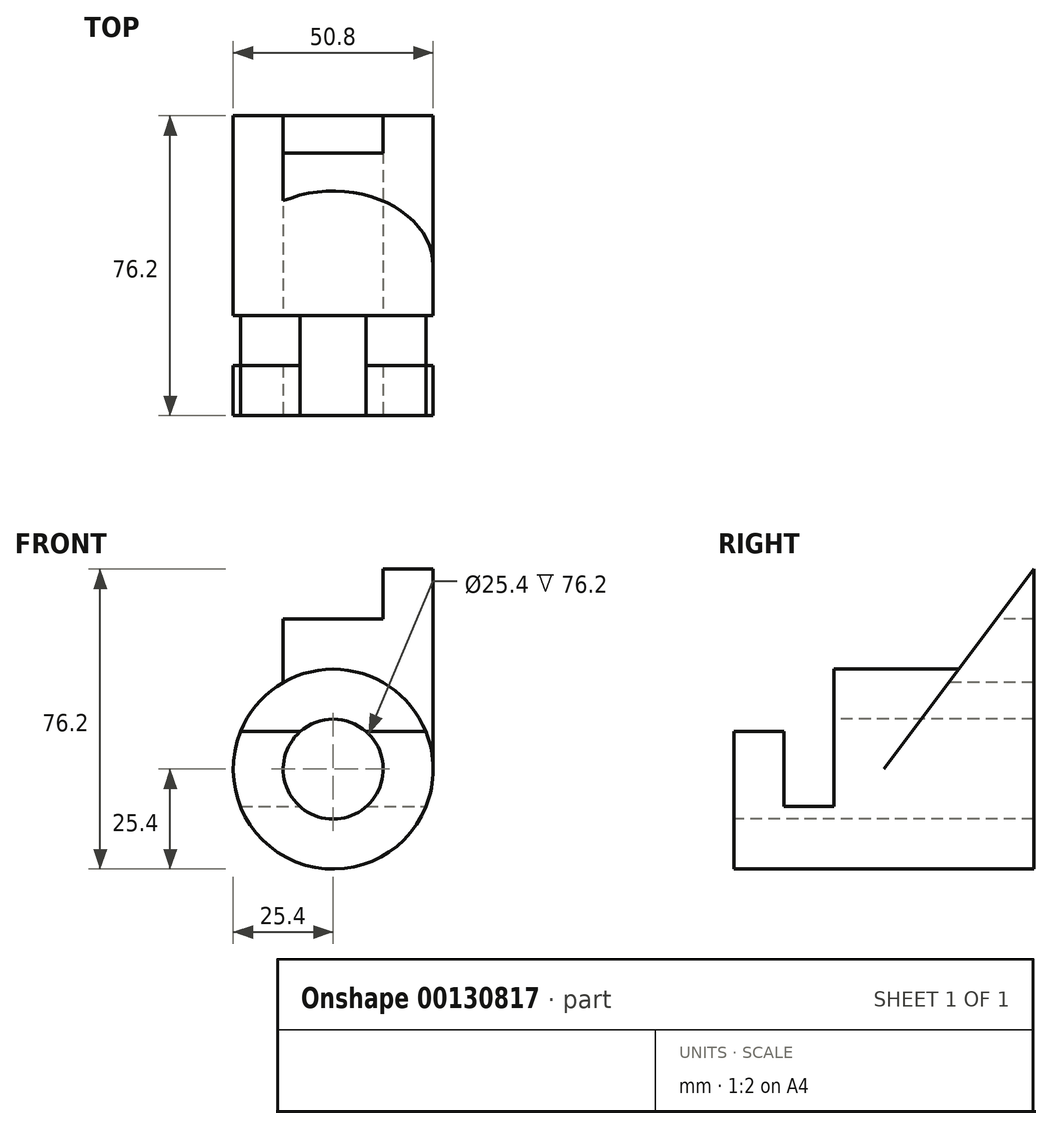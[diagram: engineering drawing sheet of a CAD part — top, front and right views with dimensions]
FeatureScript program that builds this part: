
annotation { "Feature Type Name" : "Feature", "Feature Type Description" : "" }
export const myFeature = defineFeature(function(context is Context, id is Id, definition is map)
    precondition{}
    {
        {
            var Q0;
            Q0=qCreatedBy(makeId("Front.planeOp"),FACE);
            var sketch = newSketch(context, id + "F0", { "sketchPlane" : qUnion([Q0])});
            skCircle(sketch, "E0", {"center": v(0, 0) * mm, "radius": 12.7 * mm});
            skCircle(sketch, "E1", {"center": v(0, 0) * mm, "radius": 25.4 * mm});
            skLineSegment(sketch, "E2", {"start": v(-8.4, 9.53) * mm, "end": v(-23.55, 9.53) * mm});
            skLineSegment(sketch, "E3.trimOffspring", {"start": v(8.4, 9.53) * mm, "end": v(23.55, 9.53) * mm});
            skLineSegment(sketch, "E4", {"start": v(-23.55, -9.53) * mm, "end": v(-8.4, -9.53) * mm});
            skLineSegment(sketch, "E5.trimOffspring", {"start": v(8.4, -9.53) * mm, "end": v(23.55, -9.53) * mm});
            skSolve(sketch);
        }
        {
            var Q0;
            {var subQ0=sQuery(id+"F0.wireOp",EDGE,"E2");Q0=makeQuery(id+"F0.imprint","IMPRINT",FACE,{"disambiguationData":[TD([[makeQuery(id+"F0.imprint","IMPRINT",EDGE,{"derivedFrom":subQ0}),1.0]])]});}
            var Q1;
            {var subQ0=sQuery(id+"F0.wireOp",EDGE,"E4");Q1=makeQuery(id+"F0.imprint","IMPRINT",FACE,{"disambiguationData":[TD([[makeQuery(id+"F0.imprint","IMPRINT",EDGE,{"derivedFrom":subQ0}),-1.0]])]});}
            var Q2;
            {var subQ0=sQuery(id+"F0.wireOp",EDGE,"E3.trimOffspring");Q2=makeQuery(id+"F0.imprint","IMPRINT",FACE,{"disambiguationData":[TD([[makeQuery(id+"F0.imprint","IMPRINT",EDGE,{"derivedFrom":subQ0}),-1.0]])]});}
            var Q3;
            {var subQ0=sQuery(id+"F0.wireOp",EDGE,"E2");Q3=makeQuery(id+"F0.imprint","IMPRINT",FACE,{"disambiguationData":[TD([[makeQuery(id+"F0.imprint","IMPRINT",EDGE,{"derivedFrom":subQ0}),-1.0]])]});}
            extrude(context, id + "F1", {"entities" : qUnion([Q0, Q1, Q2, Q3]), "oppositeDirection" : true, "depth" : 76.2 * mm});
        }
        {
            var Q0;
            Q0=qCreatedBy(makeId("Right.planeOp"),FACE);
            var sketch = newSketch(context, id + "F2", { "sketchPlane" : qUnion([Q0])});
            skLineSegment(sketch, "E6", {"start": v(0, 25.4) * mm, "end": v(76.2, 25.4) * mm});
            skLineSegment(sketch, "E7", {"start": v(76.2, -25.4) * mm, "end": v(0, -25.4) * mm});
            skLineSegment(sketch, "E8.0", {"start": v(0, -25.4) * mm, "end": v(0, 25.4) * mm});
            skLineSegment(sketch, "E9", {"start": v(25.4, 25.4) * mm, "end": v(25.4, -9.53) * mm});
            skLineSegment(sketch, "E10", {"start": v(25.4, -9.53) * mm, "end": v(12.7, -9.53) * mm});
            skLineSegment(sketch, "E11", {"start": v(12.7, -9.53) * mm, "end": v(12.7, 9.53) * mm});
            skLineSegment(sketch, "E12", {"start": v(12.7, 9.53) * mm, "end": v(0, 9.53) * mm});
            skSolve(sketch);
        }
        {
            var Q0;
            {var subQ4=sQuery(id+"F2.wireOp",EDGE,"E9");Q0=makeQuery(id+"F2.imprint","IMPRINT",FACE,{"disambiguationData":[TD([[makeQuery(id+"F2.imprint","IMPRINT",EDGE,{"derivedFrom":subQ4}),-1.0]])]});}
            extrude(context, id + "F3", {"entities" : qUnion([Q0]), "operationType" : NewBodyOperationType.REMOVE, "endBound" : BoundingType.SYMMETRIC, "oppositeDirection" : true, "depth" : 50.8 * mm});
        }
        {
            var Q0;
            Q0=qCreatedBy(makeId("Right.planeOp"),FACE);
            var sketch = newSketch(context, id + "F4", { "sketchPlane" : qUnion([Q0])});
            skLineSegment(sketch, "E13.0", {"start": v(76.2, -25.4) * mm, "end": v(76.2, 25.4) * mm});
            skLineSegment(sketch, "E14", {"start": v(76.2, 0) * mm, "end": v(76.2, 50.8) * mm});
            skLineSegment(sketch, "E15", {"start": v(76.2, 0) * mm, "end": v(38.1, 0) * mm});
            skLineSegment(sketch, "E16", {"start": v(38.1, 0) * mm, "end": v(76.2, 50.8) * mm});
            skSolve(sketch);
        }
        {
            var Q0;
            {var subQ0=sQuery(id+"F4.wireOp",EDGE,"E15");Q0=makeQuery(id+"F4.imprint","IMPRINT",FACE,{"disambiguationData":[TD([[makeQuery(id+"F4.imprint","IMPRINT",EDGE,{"derivedFrom":subQ0}),-1.0]])]});}
            extrude(context, id + "F5", {"entities" : qUnion([Q0]), "operationType" : NewBodyOperationType.ADD, "depth" : 25.4 * mm, "hasSecondDirection" : true, "secondDirectionOppositeDirection" : true, "secondDirectionDepth" : 12.7 * mm});
        }
        {
            var Q0;
            Q0=makeQuery(id+"F5.opExtrude","CAP_FACE",FACE,{"disambiguationData":[OSD([sQuery(id+"F4.wireOp",EDGE,"E14"),sQuery(id+"F4.wireOp",EDGE,"E15"),sQuery(id+"F4.wireOp",EDGE,"E16")])],"isStart":true});
            var sketch = newSketch(context, id + "F6", { "sketchPlane" : qUnion([Q0])});
            skLineSegment(sketch, "E17", {"start": v(-76.2, 38.1) * mm, "end": v(-66.68, 38.1) * mm});
            skSolve(sketch);
        }
        {
            var Q0;
            {var subQ0=sQuery(id+"F6.wireOp",EDGE,"E17");Q0=makeQuery(id+"F6.imprint","IMPRINT",FACE,{"disambiguationData":[TD([[makeQuery(id+"F6.imprint","IMPRINT",EDGE,{"derivedFrom":subQ0}),1.0]])]});}
            extrude(context, id + "F7", {"entities" : qUnion([Q0]), "operationType" : NewBodyOperationType.REMOVE, "oppositeDirection" : true, "depth" : 25.4 * mm});
        }
        {
            var Q0;
            Q0=makeQuery(id+"F5.boolean.opBoolean","MERGE",FACE,{"derivedFrom":[makeQuery(id+"F1.opExtrude","CAP_FACE",FACE,{"disambiguationData":[OSD([sQuery(id+"F0.wireOp",EDGE,"E0"),sQuery(id+"F0.wireOp",EDGE,"E1")])],"isStart":false}),makeQuery(id+"F5.opExtrude","SWEPT_FACE",FACE,{"disambiguationData":[OSD([sQuery(id+"F4.wireOp",EDGE,"E14")])]})]});
            var sketch = newSketch(context, id + "F8", { "sketchPlane" : qUnion([Q0])});
            skCircle(sketch, "E18", {"center": v(0, 0) * mm, "radius": 12.7 * mm});
            skSolve(sketch);
        }
        {
            var Q0;
            Q0 = qSketchRegion(id + "F8", true);
            var Q1;
            Q1=makeQuery(id+"F8.imprint","IMPRINT",FACE,{"disambiguationData":[TD([[makeQuery(id+"F8.imprint","IMPRINT",EDGE,{"disambiguationData":[OD(0.0)],"derivedFrom":sQuery(id+"F8.wireOp",EDGE,"E18")}),1.0]])]});
            extrude(context, id + "F9", {"entities" : qUnion([Q0, Q1]), "operationType" : NewBodyOperationType.REMOVE, "endBound" : BoundingType.THROUGH_ALL, "oppositeDirection" : true, "depth" : 25.4 * mm});
        }
    });
